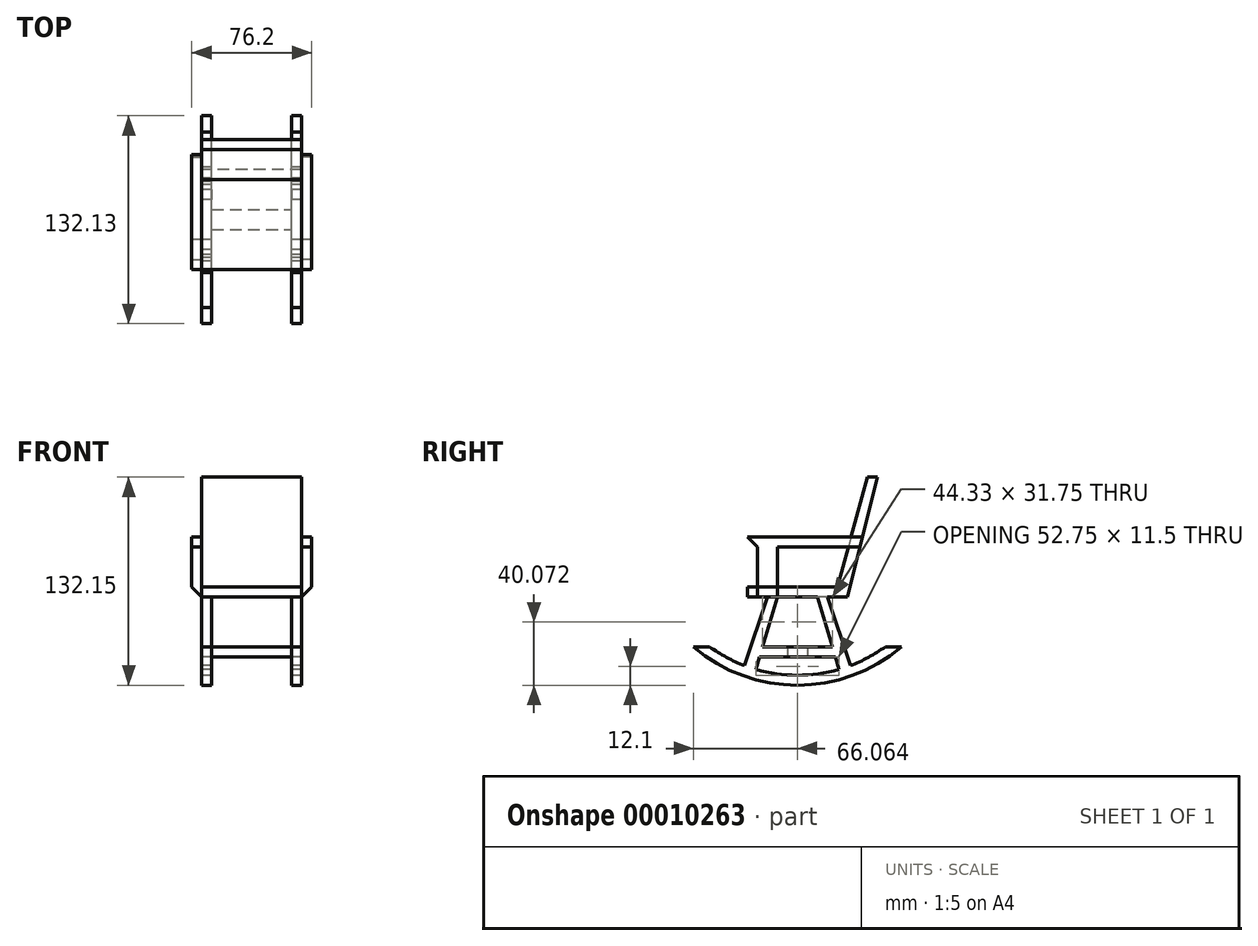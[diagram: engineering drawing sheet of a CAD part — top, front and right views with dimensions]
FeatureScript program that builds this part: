
annotation { "Feature Type Name" : "Feature", "Feature Type Description" : "" }
export const myFeature = defineFeature(function(context is Context, id is Id, definition is map)
    precondition{}
    {
        {
            var Q0;
            Q0=qCreatedBy(makeId("Right.planeOp"),FACE);
            var sketch = newSketch(context, id + "F0", { "sketchPlane" : qUnion([Q0])});
            skLineSegment(sketch, "E0.top", {"start": v(-26.93, -42.05) * mm, "end": v(21.2, -42.05) * mm});
            skLineSegment(sketch, "E0.left", {"start": v(-34.62, 2.4) * mm, "end": v(-34.62, -3.95) * mm});
            skLineSegment(sketch, "E1", {"start": v(-34.62, -3.95) * mm, "end": v(-21.92, -3.95) * mm});
            skLineSegment(sketch, "E2", {"start": v(-21.92, -3.95) * mm, "end": v(-34.62, -42.05) * mm});
            skLineSegment(sketch, "E3", {"start": v(16.18, -3.95) * mm, "end": v(28.88, -42.05) * mm});
            skLineSegment(sketch, "E4", {"start": v(-15.57, -3.95) * mm, "end": v(-25.03, -35.7) * mm});
            skLineSegment(sketch, "E5", {"start": v(9.83, -3.95) * mm, "end": v(19.3, -35.7) * mm});
            skLineSegment(sketch, "E6.0", {"start": v(-25.03, -35.7) * mm, "end": v(19.3, -35.7) * mm});
            skLineSegment(sketch, "E7.0", {"start": v(-34.62, 2.4) * mm, "end": v(22.53, 2.4) * mm});
            skPoint(sketch, "E8.orphan", {"position": v(-34.62, 34.15) * mm});
            skLineSegment(sketch, "E9.trimOffspring", {"start": v(-15.57, -3.95) * mm, "end": v(9.83, -3.95) * mm});
            skLineSegment(sketch, "E10.trimOffspring", {"start": v(21.2, -42.05) * mm, "end": v(22.53, -46.55) * mm});
            skLineSegment(sketch, "E11.trimOffspring", {"start": v(-26.93, -42.05) * mm, "end": v(-28.27, -46.55) * mm});
            skLineSegment(sketch, "E12.trimOffspring", {"start": v(16.18, -3.95) * mm, "end": v(28.88, -3.95) * mm});
            skLineSegment(sketch, "E13", {"start": v(41.58, 72.25) * mm, "end": v(22.53, 2.4) * mm});
            skLineSegment(sketch, "E14", {"start": v(47.93, 72.25) * mm, "end": v(28.88, -3.95) * mm});
            skLineSegment(sketch, "E15", {"start": v(41.58, 72.25) * mm, "end": v(47.93, 72.25) * mm});
            skArc(sketch, "E16", {"start": v(-68.93, -35.49) * mm, "mid": v(-2.87, -59.9) * mm, "end": v(63.2, -35.49) * mm});
            skArc(sketch, "E17", {"start": v(-58.67, -35.49) * mm, "mid": v(-2.87, -53.55) * mm, "end": v(52.94, -35.49) * mm});
            skLineSegment(sketch, "E18", {"start": v(-21.92, -3.95) * mm, "end": v(-36.41, -47.44) * mm});
            skLineSegment(sketch, "E19", {"start": v(63.2, -35.49) * mm, "end": v(52.94, -35.49) * mm});
            skLineSegment(sketch, "E20.MirrorCS", {"start": v(-68.93, -35.49) * mm, "end": v(-58.67, -35.49) * mm});
            skPoint(sketch, "E21.center.orphan", {"position": v(-2.87, -3.95) * mm});
            skPoint(sketch, "E22.orphan", {"position": v(-55, -24.24) * mm});
            skLineSegment(sketch, "E23", {"start": v(16.18, -3.95) * mm, "end": v(30.68, -47.44) * mm});
            skPoint(sketch, "E24.orphan", {"position": v(49.27, -24.24) * mm});
            skPoint(sketch, "E25.MirrorCS.end.orphan", {"position": v(-68.93, -35.49) * mm});
            skLineSegment(sketch, "E26.trimOffspring", {"start": v(-26.93, -42.05) * mm, "end": v(-29.24, -49.82) * mm});
            skLineSegment(sketch, "E27.trimOffspring", {"start": v(21.2, -42.05) * mm, "end": v(23.5, -49.82) * mm});
            skSolve(sketch);
        }
        {
            var Q0;
            Q0 = qSketchRegion(id + "F0", true);
            extrude(context, id + "F1", {"entities" : qUnion([Q0]), "depth" : 63.5 * mm});
        }
        {
            var Q0;
            Q0=makeQuery(id+"F1.opExtrude","SWEPT_FACE",FACE,{"disambiguationData":[OSD([sQuery(id+"F0.wireOp",EDGE,"E7.0")])]});
            var sketch = newSketch(context, id + "F2", { "sketchPlane" : qUnion([Q0])});
            skLineSegment(sketch, "E28", {"start": v(57.15, -15.57) * mm, "end": v(57.15, 9.83) * mm});
            skLineSegment(sketch, "E29", {"start": v(57.15, 9.83) * mm, "end": v(6.35, 9.83) * mm});
            skLineSegment(sketch, "E30", {"start": v(6.35, -15.57) * mm, "end": v(57.15, -15.57) * mm});
            skLineSegment(sketch, "E31.0", {"start": v(6.35, -15.57) * mm, "end": v(6.35, 9.83) * mm});
            skPoint(sketch, "E32.start.orphan", {"position": v(0, -15.57) * mm});
            skPoint(sketch, "E33.orphan", {"position": v(0, 9.83) * mm});
            skSolve(sketch);
        }
        {
            var Q0;
            Q0 = qSketchRegion(id + "F2", true);
            extrude(context, id + "F3", {"entities" : qUnion([Q0]), "operationType" : NewBodyOperationType.REMOVE, "oppositeDirection" : true, "depth" : 66.74 * mm});
        }
        {
            var Q0;
            Q0=makeQuery(id+"F3.boolean.opBoolean","COPY",FACE,{"disambiguationData":[TD([makeQuery(id+"F1.opExtrude","SWEPT_FACE",FACE,{"disambiguationData":[OSD([sQuery(id+"F0.wireOp",EDGE,"E7.0")])]})])],"derivedFrom":makeQuery(id+"F3.opExtrude","SWEPT_FACE",FACE,{"disambiguationData":[OSD([sQuery(id+"F2.wireOp",EDGE,"E29")])]})});
            var sketch = newSketch(context, id + "F4", { "sketchPlane" : qUnion([Q0])});
            skLineSegment(sketch, "E34.bottom", {"start": v(6.35, 2.4) * mm, "end": v(57.15, 2.4) * mm});
            skLineSegment(sketch, "E34.top", {"start": v(6.35, -3.95) * mm, "end": v(57.15, -3.95) * mm});
            skLineSegment(sketch, "E34.left", {"start": v(6.35, 2.4) * mm, "end": v(6.35, -3.95) * mm});
            skLineSegment(sketch, "E34.right", {"start": v(57.15, 2.4) * mm, "end": v(57.15, -3.95) * mm});
            skSolve(sketch);
        }
        {
            var Q0;
            Q0 = qSketchRegion(id + "F4", true);
            extrude(context, id + "F5", {"entities" : qUnion([Q0]), "operationType" : NewBodyOperationType.ADD, "depth" : 32.98 * mm});
        }
        {
            var Q0;
            {var subQ15=sQuery(id+"F0.wireOp",EDGE,"E9.trimOffspring");var subQ24=makeQuery(id+"F1.opExtrude","SWEPT_FACE",FACE,{"disambiguationData":[OSD([subQ15])]});Q0=makeQuery(id+"F5.boolean.opBoolean","MERGE",FACE,{"derivedFrom":[makeQuery(id+"F3.boolean.opBoolean","SPLIT",FACE,{"disambiguationData":[TD([makeQuery(id+"F3.opExtrude","SWEPT_FACE",FACE,{"disambiguationData":[OSD([sQuery(id+"F2.wireOp",EDGE,"E31.0")])]})])],"derivedFrom":subQ24}),makeQuery(id+"F3.boolean.opBoolean","SPLIT",FACE,{"disambiguationData":[TD([makeQuery(id+"F3.opExtrude","SWEPT_FACE",FACE,{"disambiguationData":[OSD([sQuery(id+"F2.wireOp",EDGE,"E28")])]})])],"derivedFrom":subQ24}),makeQuery(id+"F5.opExtrude","SWEPT_FACE",FACE,{"disambiguationData":[OSD([sQuery(id+"F4.wireOp",EDGE,"E34.top")])]})]});}
            var sketch = newSketch(context, id + "F6", { "sketchPlane" : qUnion([Q0])});
            skLineSegment(sketch, "E35", {"start": v(63.5, 2.87) * mm, "end": v(0, 2.87) * mm});
            skLineSegment(sketch, "E36", {"start": v(63.5, 9.22) * mm, "end": v(0, 9.22) * mm});
            skLineSegment(sketch, "E37.0", {"start": v(57.15, 15.57) * mm, "end": v(57.15, 2.87) * mm});
            skLineSegment(sketch, "E38.0", {"start": v(6.35, 9.22) * mm, "end": v(6.35, 2.87) * mm});
            skSolve(sketch);
        }
        {
            var Q0;
            {var subQ0=sQuery(id+"F6.wireOp",EDGE,"E38.0");Q0=makeQuery(id+"F6.imprint","IMPRINT",FACE,{"disambiguationData":[TD([[makeQuery(id+"F6.imprint","IMPRINT",EDGE,{"derivedFrom":subQ0}),1.0]])]});}
            extrude(context, id + "F7", {"entities" : qUnion([Q0]), "operationType" : NewBodyOperationType.ADD, "depth" : 65.56 * mm});
        }
        {
            var Q0;
            Q0=makeQuery(id+"F7.opExtrude","SWEPT_FACE",FACE,{"disambiguationData":[OSD([sQuery(id+"F6.wireOp",EDGE,"E36")])]});
            var sketch = newSketch(context, id + "F8", { "sketchPlane" : qUnion([Q0])});
            skLineSegment(sketch, "E39.bottom", {"start": v(57.15, -3.95) * mm, "end": v(6.35, -3.95) * mm});
            skLineSegment(sketch, "E39.top", {"start": v(57.15, -69.51) * mm, "end": v(6.35, -69.51) * mm});
            skLineSegment(sketch, "E39.left", {"start": v(57.15, -3.95) * mm, "end": v(57.15, -69.51) * mm});
            skLineSegment(sketch, "E39.right", {"start": v(6.35, -3.95) * mm, "end": v(6.35, -69.51) * mm});
            skSolve(sketch);
        }
        {
            var Q0;
            {var subQ2=sQuery(id+"F8.wireOp",EDGE,"E39.bottom");Q0=makeQuery(id+"F8.imprint","IMPRINT",FACE,{"disambiguationData":[TD([[makeQuery(id+"F8.imprint","IMPRINT",EDGE,{"derivedFrom":subQ2}),1.0]])]});}
            extrude(context, id + "F9", {"entities" : qUnion([Q0]), "operationType" : NewBodyOperationType.REMOVE, "depth" : 91.35 * mm});
        }
        {
            var Q0;
            Q0=makeQuery(id+"F7.opExtrude","SWEPT_FACE",FACE,{"disambiguationData":[OSD([sQuery(id+"F6.wireOp",EDGE,"E36")])]});
            extrude(context, id + "F10", {"entities" : qUnion([Q0]), "operationType" : NewBodyOperationType.REMOVE, "oppositeDirection" : true, "depth" : 101.17 * mm});
        }
        {
            var Q0;
            Q0=makeQuery(id+"F1.opExtrude","CAP_FACE",FACE,{"disambiguationData":[OSD([sQuery(id+"F0.wireOp",EDGE,"E0.top"),sQuery(id+"F0.wireOp",EDGE,"E0.left"),sQuery(id+"F0.wireOp",EDGE,"E1"),sQuery(id+"F0.wireOp",EDGE,"E21"),sQuery(id+"F0.wireOp",EDGE,"E2"),sQuery(id+"F0.wireOp",EDGE,"E3"),sQuery(id+"F0.wireOp",EDGE,"E4"),sQuery(id+"F0.wireOp",EDGE,"E5"),sQuery(id+"F0.wireOp",EDGE,"E6.0"),sQuery(id+"F0.wireOp",EDGE,"E7.0"),sQuery(id+"F0.wireOp",EDGE,"270e6304-8c91-43a8-9c8a-24b8539c111a.0"),sQuery(id+"F0.wireOp",EDGE,"771b2fe0-ea7f-4f7a-b607-9c96d6c6b4a5"),sQuery(id+"F0.wireOp",EDGE,"dd6d9a9d-6ea5-439d-bcf5-dbf2de2fa210.trimOffspring"),sQuery(id+"F0.wireOp",EDGE,"E9.trimOffspring"),sQuery(id+"F0.wireOp",EDGE,"b3621c98-222f-4a81-ac37-0409976ba373.trimOffspring"),sQuery(id+"F0.wireOp",EDGE,"e584de07-e880-4e55-a246-7a31de8ac933.trimOffspring"),sQuery(id+"F0.wireOp",EDGE,"E10.trimOffspring"),sQuery(id+"F0.wireOp",EDGE,"E11.trimOffspring"),sQuery(id+"F0.wireOp",EDGE,"E12.trimOffspring"),sQuery(id+"F0.wireOp",EDGE,"E13"),sQuery(id+"F0.wireOp",EDGE,"E14"),sQuery(id+"F0.wireOp",EDGE,"E15")])],"isStart":false});
            var sketch = newSketch(context, id + "F11", { "sketchPlane" : qUnion([Q0])});
            skLineSegment(sketch, "E40", {"start": v(-25.03, -35.7) * mm, "end": v(-25.03, -35.7) * mm});
            skLineSegment(sketch, "E41.0", {"start": v(-9.22, -35.7) * mm, "end": v(-9.22, -42.05) * mm});
            skLineSegment(sketch, "E42.0", {"start": v(3.48, -35.7) * mm, "end": v(3.48, -42.05) * mm});
            skLineSegment(sketch, "E43", {"start": v(-9.22, -35.7) * mm, "end": v(3.48, -35.7) * mm});
            skLineSegment(sketch, "E44", {"start": v(3.48, -42.05) * mm, "end": v(-9.22, -42.05) * mm});
            skSolve(sketch);
        }
        {
            var Q0;
            Q0 = qSketchRegion(id + "F11", true);
            extrude(context, id + "F12", {"entities" : qUnion([Q0]), "operationType" : NewBodyOperationType.ADD, "oppositeDirection" : true, "depth" : 60.56 * mm});
        }
        {
            var Q0;
            Q0=makeQuery(id+"F1.opExtrude","CAP_FACE",FACE,{"disambiguationData":[OSD([sQuery(id+"F0.wireOp",EDGE,"E0.top"),sQuery(id+"F0.wireOp",EDGE,"E0.left"),sQuery(id+"F0.wireOp",EDGE,"E1"),sQuery(id+"F0.wireOp",EDGE,"E21"),sQuery(id+"F0.wireOp",EDGE,"E2"),sQuery(id+"F0.wireOp",EDGE,"E3"),sQuery(id+"F0.wireOp",EDGE,"E4"),sQuery(id+"F0.wireOp",EDGE,"E5"),sQuery(id+"F0.wireOp",EDGE,"E6.0"),sQuery(id+"F0.wireOp",EDGE,"E7.0"),sQuery(id+"F0.wireOp",EDGE,"270e6304-8c91-43a8-9c8a-24b8539c111a.0"),sQuery(id+"F0.wireOp",EDGE,"771b2fe0-ea7f-4f7a-b607-9c96d6c6b4a5"),sQuery(id+"F0.wireOp",EDGE,"dd6d9a9d-6ea5-439d-bcf5-dbf2de2fa210.trimOffspring"),sQuery(id+"F0.wireOp",EDGE,"E9.trimOffspring"),sQuery(id+"F0.wireOp",EDGE,"b3621c98-222f-4a81-ac37-0409976ba373.trimOffspring"),sQuery(id+"F0.wireOp",EDGE,"e584de07-e880-4e55-a246-7a31de8ac933.trimOffspring"),sQuery(id+"F0.wireOp",EDGE,"E10.trimOffspring"),sQuery(id+"F0.wireOp",EDGE,"E11.trimOffspring"),sQuery(id+"F0.wireOp",EDGE,"E12.trimOffspring"),sQuery(id+"F0.wireOp",EDGE,"E13"),sQuery(id+"F0.wireOp",EDGE,"E14"),sQuery(id+"F0.wireOp",EDGE,"E15")])],"isStart":false});
            var sketch = newSketch(context, id + "F13", { "sketchPlane" : qUnion([Q0])});
            skLineSegment(sketch, "E45", {"start": v(-15.57, -3.95) * mm, "end": v(-15.57, 27.8) * mm});
            skLineSegment(sketch, "E46", {"start": v(-15.57, 27.8) * mm, "end": v(36.82, 27.8) * mm});
            skLineSegment(sketch, "E47", {"start": v(-34.62, 34.15) * mm, "end": v(38.4, 34.15) * mm});
            skLineSegment(sketch, "E48", {"start": v(38.4, 34.15) * mm, "end": v(36.82, 27.8) * mm});
            skLineSegment(sketch, "E49", {"start": v(-28.27, 27.8) * mm, "end": v(-34.62, 34.15) * mm});
            skLineSegment(sketch, "E50", {"start": v(-28.27, -3.95) * mm, "end": v(-15.57, -3.95) * mm});
            skLineSegment(sketch, "E51", {"start": v(-28.27, 27.8) * mm, "end": v(-28.27, -3.95) * mm});
            skSolve(sketch);
        }
        {
            var Q0;
            Q0 = qSketchRegion(id + "F13", true);
            extrude(context, id + "F14", {"entities" : qUnion([Q0]), "operationType" : NewBodyOperationType.ADD, "depth" : 6.35 * mm});
        }
        {
            var Q0;
            Q0=makeQuery(id+"F1.opExtrude","CAP_FACE",FACE,{"disambiguationData":[OSD([sQuery(id+"F0.wireOp",EDGE,"E0.top"),sQuery(id+"F0.wireOp",EDGE,"E0.left"),sQuery(id+"F0.wireOp",EDGE,"E1"),sQuery(id+"F0.wireOp",EDGE,"E21"),sQuery(id+"F0.wireOp",EDGE,"E2"),sQuery(id+"F0.wireOp",EDGE,"E3"),sQuery(id+"F0.wireOp",EDGE,"E4"),sQuery(id+"F0.wireOp",EDGE,"E5"),sQuery(id+"F0.wireOp",EDGE,"E6.0"),sQuery(id+"F0.wireOp",EDGE,"E7.0"),sQuery(id+"F0.wireOp",EDGE,"270e6304-8c91-43a8-9c8a-24b8539c111a.0"),sQuery(id+"F0.wireOp",EDGE,"771b2fe0-ea7f-4f7a-b607-9c96d6c6b4a5"),sQuery(id+"F0.wireOp",EDGE,"dd6d9a9d-6ea5-439d-bcf5-dbf2de2fa210.trimOffspring"),sQuery(id+"F0.wireOp",EDGE,"E9.trimOffspring"),sQuery(id+"F0.wireOp",EDGE,"b3621c98-222f-4a81-ac37-0409976ba373.trimOffspring"),sQuery(id+"F0.wireOp",EDGE,"e584de07-e880-4e55-a246-7a31de8ac933.trimOffspring"),sQuery(id+"F0.wireOp",EDGE,"E10.trimOffspring"),sQuery(id+"F0.wireOp",EDGE,"E11.trimOffspring"),sQuery(id+"F0.wireOp",EDGE,"E12.trimOffspring"),sQuery(id+"F0.wireOp",EDGE,"E13"),sQuery(id+"F0.wireOp",EDGE,"E14"),sQuery(id+"F0.wireOp",EDGE,"E15")])],"isStart":true});
            var sketch = newSketch(context, id + "F15", { "sketchPlane" : qUnion([Q0])});
            skLineSegment(sketch, "E52", {"start": v(15.57, -3.95) * mm, "end": v(15.57, 27.8) * mm});
            skLineSegment(sketch, "E53", {"start": v(34.62, 34.15) * mm, "end": v(-38.4, 34.15) * mm});
            skLineSegment(sketch, "E54", {"start": v(15.57, 27.8) * mm, "end": v(-36.82, 27.8) * mm});
            skLineSegment(sketch, "E55", {"start": v(-36.82, 27.8) * mm, "end": v(-38.4, 34.15) * mm});
            skLineSegment(sketch, "E56", {"start": v(34.62, 34.15) * mm, "end": v(28.27, 27.8) * mm});
            skLineSegment(sketch, "E57", {"start": v(28.27, -3.95) * mm, "end": v(15.57, -3.95) * mm});
            skLineSegment(sketch, "E58", {"start": v(28.27, 27.8) * mm, "end": v(28.27, -3.95) * mm});
            skSolve(sketch);
        }
        {
            var Q0;
            Q0 = qSketchRegion(id + "F15", true);
            extrude(context, id + "F16", {"entities" : qUnion([Q0]), "operationType" : NewBodyOperationType.ADD, "depth" : 6.35 * mm});
        }
        {
            var Q0;
            Q0=makeQuery(id+"F16.opExtrude","SWEPT_FACE",FACE,{"disambiguationData":[OSD([sQuery(id+"F15.wireOp",EDGE,"E58")])]});
            var sketch = newSketch(context, id + "F17", { "sketchPlane" : qUnion([Q0])});
            skLineSegment(sketch, "E59", {"start": v(-6.35, 2.4) * mm, "end": v(-6.35, -3.95) * mm});
            skLineSegment(sketch, "E60", {"start": v(-6.35, -3.95) * mm, "end": v(0, -3.95) * mm});
            skLineSegment(sketch, "E61", {"start": v(-6.35, 2.4) * mm, "end": v(0, -3.95) * mm});
            skLineSegment(sketch, "E62.MirrorCS", {"start": v(69.85, 2.4) * mm, "end": v(69.85, -3.95) * mm});
            skLineSegment(sketch, "E63.MirrorCS", {"start": v(69.85, 2.4) * mm, "end": v(63.5, -3.95) * mm});
            skLineSegment(sketch, "E64.MirrorCS", {"start": v(69.85, -3.95) * mm, "end": v(63.5, -3.95) * mm});
            skSolve(sketch);
        }
        {
            var Q0;
            Q0 = qSketchRegion(id + "F17", true);
            extrude(context, id + "F18", {"entities" : qUnion([Q0]), "operationType" : NewBodyOperationType.REMOVE, "endBound" : BoundingType.THROUGH_ALL, "oppositeDirection" : true, "depth" : 25.4 * mm});
        }
    });
